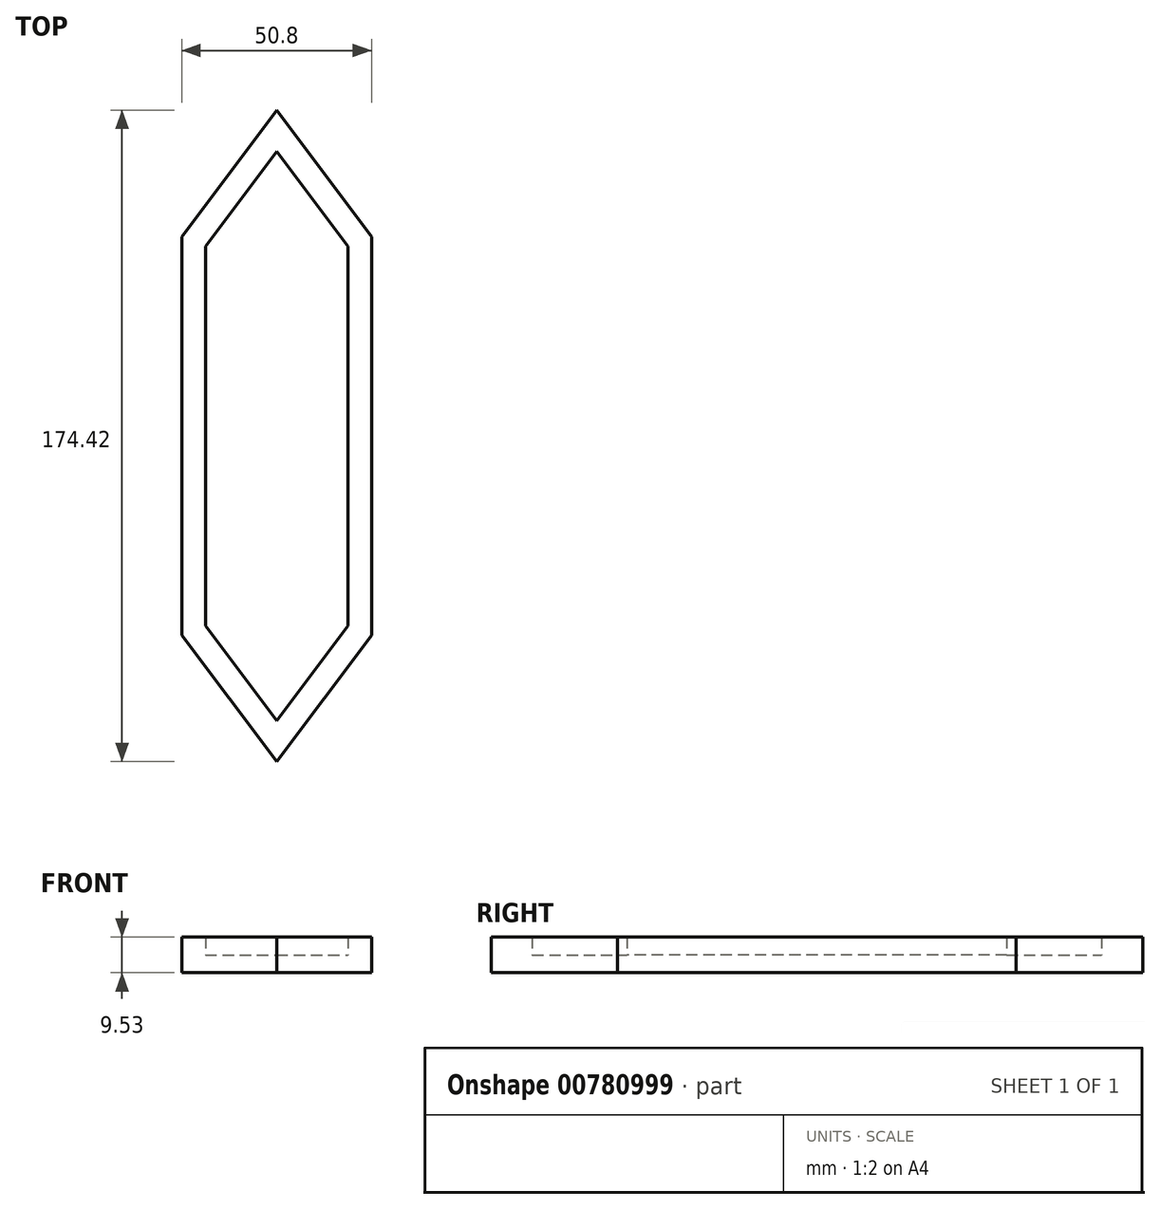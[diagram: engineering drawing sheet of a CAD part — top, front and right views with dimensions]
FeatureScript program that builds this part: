
annotation { "Feature Type Name" : "Feature", "Feature Type Description" : "" }
export const myFeature = defineFeature(function(context is Context, id is Id, definition is map)
    precondition{}
    {
        {
            var Q0;
            Q0=qCreatedBy(makeId("Top.planeOp"),FACE);
            var sketch = newSketch(context, id + "F0", { "sketchPlane" : qUnion([Q0])});
            skLineSegment(sketch, "E0.left", {"start": v(-19.05, 50.8) * mm, "end": v(-19.05, -50.8) * mm});
            skLineSegment(sketch, "E0.right", {"start": v(19.05, 50.8) * mm, "end": v(19.05, -50.8) * mm});
            skPoint(sketch, "E0.middle", {"position": v(0, 0) * mm});
            skLineSegment(sketch, "E1.left", {"start": v(-25.4, 53.34) * mm, "end": v(-25.4, -53.34) * mm});
            skLineSegment(sketch, "E1.right", {"start": v(25.4, 53.34) * mm, "end": v(25.4, -53.34) * mm});
            skLineSegment(sketch, "E2", {"start": v(-19.05, 50.8) * mm, "end": v(0, 76.2) * mm});
            skLineSegment(sketch, "E3", {"start": v(0, 76.2) * mm, "end": v(19.05, 50.8) * mm});
            skLineSegment(sketch, "E4", {"start": v(-25.4, 53.34) * mm, "end": v(0, 87.2) * mm});
            skLineSegment(sketch, "E5", {"start": v(0, 87.2) * mm, "end": v(25.4, 53.34) * mm});
            skLineSegment(sketch, "E6", {"start": v(-19.05, -50.8) * mm, "end": v(0, -76.2) * mm});
            skLineSegment(sketch, "E7", {"start": v(0, -76.2) * mm, "end": v(19.05, -50.8) * mm});
            skLineSegment(sketch, "E8", {"start": v(-25.4, -53.34) * mm, "end": v(0, -87.2) * mm});
            skLineSegment(sketch, "E9", {"start": v(0, -87.2) * mm, "end": v(25.4, -53.34) * mm});
            skSolve(sketch);
        }
        {
            var Q0;
            Q0=makeQuery(id+"F0.imprint","IMPRINT",FACE,{"disambiguationData":[TD([[makeQuery(id+"F0.imprint","IMPRINT",EDGE,{"derivedFrom":sQuery(id+"F0.wireOp",EDGE,"E0.bottom")}),1.0]])]});
            var Q1;
            Q1=makeQuery(id+"F0.imprint","IMPRINT",FACE,{"disambiguationData":[TD([[makeQuery(id+"F0.imprint","IMPRINT",EDGE,{"derivedFrom":sQuery(id+"F0.wireOp",EDGE,"E0.left")}),-1.0]])]});
            extrude(context, id + "F1", {"entities" : qUnion([Q0, Q1]), "depth" : 9.52 * mm, "offsetDistance" : 25.4 * mm});
        }
        {
            var Q0;
            Q0=makeQuery(id+"F0.imprint","IMPRINT",FACE,{"disambiguationData":[TD([[makeQuery(id+"F0.imprint","IMPRINT",EDGE,{"derivedFrom":sQuery(id+"F0.wireOp",EDGE,"E0.bottom")}),-1.0]])]});
            var Q1;
            Q1=makeQuery(id+"F0.imprint","IMPRINT",FACE,{"disambiguationData":[TD([[makeQuery(id+"F0.imprint","IMPRINT",EDGE,{"derivedFrom":sQuery(id+"F0.wireOp",EDGE,"E0.left")}),1.0]])]});
            extrude(context, id + "F2", {"entities" : qUnion([Q0, Q1]), "operationType" : NewBodyOperationType.ADD, "depth" : 4.76 * mm, "offsetDistance" : 25.4 * mm});
        }
    });
